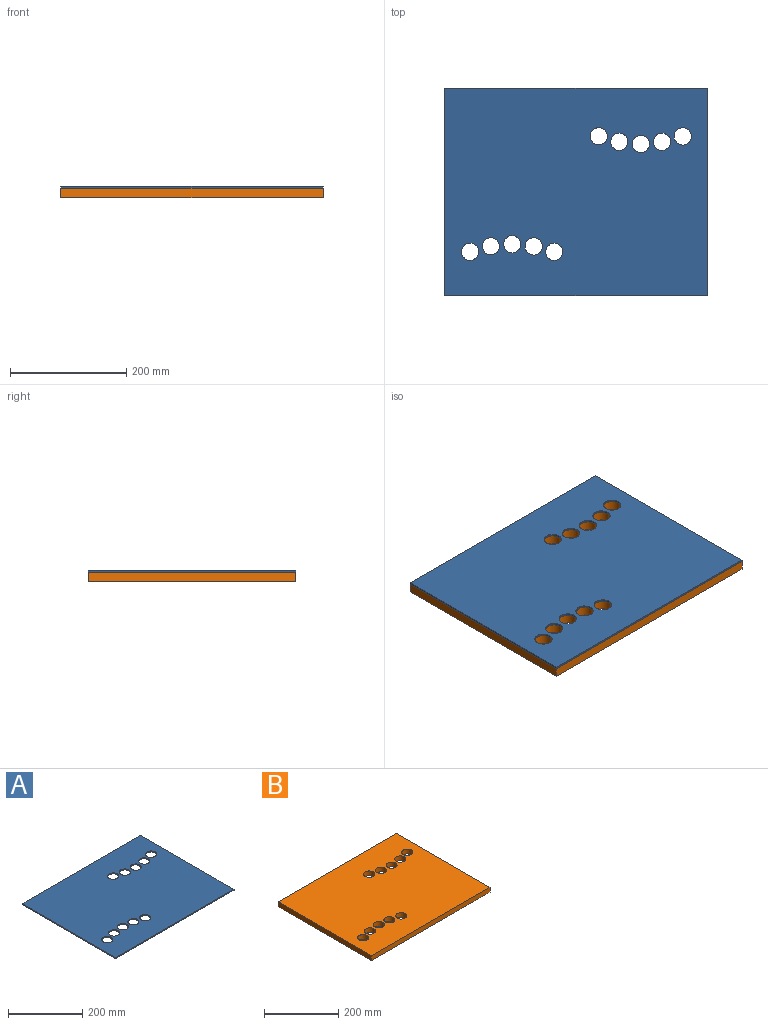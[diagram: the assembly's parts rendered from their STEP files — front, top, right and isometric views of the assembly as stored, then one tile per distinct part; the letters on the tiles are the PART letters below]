
ASSEMBLY  parts=2 mates=1
PART A: 16 faces, bbox 450.9x355.6x3.2 mm
  f0: plane 450.85x3.18mm, normal (0,1,0), area 1431.4mm2, adj f1,f8,f9,f10
  f1: plane 355.6x3.18mm, normal (-1,0,0), area 1129mm2, adj f0,f2,f9,f10
  f2: plane 450.85x3.18mm, normal (0,-1,0), area 1431.4mm2, adj f1,f8,f9,f10
  f3: cylinder r=14.87mm len=29.73mm, axis (0,0,1), area 296.6mm2, adj f9,f10
  f4: cylinder r=14.75mm len=29.5mm, axis (0,0,1), area 294.3mm2, adj f9,f10
  f5: cylinder r=14.76mm len=29.51mm, axis (0,0,1), area 294.4mm2, adj f9,f10
  f6: cylinder r=14.87mm len=29.73mm, axis (0,0,1), area 296.6mm2, adj f9,f10
  f7: cylinder r=14.8mm len=29.6mm, axis (0,0,1), area 295.3mm2, adj f9,f10
  f8: plane 355.6x3.18mm, normal (1,0,0), area 1129mm2, adj f0,f2,f9,f10
  f9: plane 450.85x355.6mm, normal (0,0,-1), area 153433.5mm2, adj f0,f1,f2,f3,f4,f5,f6,f7
  f10: plane 450.85x355.6mm, normal (0,0,1), area 153433.5mm2, adj f0,f1,f2,f3,f4,f5,f6,f7
  f11: cylinder r=14.87mm len=29.73mm, axis (0,0,1), area 296.6mm2, adj f9,f10
  f12: cylinder r=14.75mm len=29.5mm, axis (0,0,1), area 294.3mm2, adj f9,f10
  f13: cylinder r=14.76mm len=29.51mm, axis (0,0,1), area 294.4mm2, adj f9,f10
  f14: cylinder r=14.87mm len=29.73mm, axis (0,0,1), area 296.6mm2, adj f9,f10
  f15: cylinder r=14.8mm len=29.6mm, axis (0,0,1), area 295.3mm2, adj f9,f10
PART B: 16 faces, bbox 450.9x355.6x15.9 mm
  f0: plane 450.85x15.88mm, normal (0,1,0), area 7157.2mm2, adj f1,f13,f14,f15
  f1: plane 355.6x15.88mm, normal (1,0,0), area 5645.2mm2, adj f0,f2,f14,f15
  f2: plane 450.85x15.88mm, normal (0,-1,0), area 7157.2mm2, adj f1,f13,f14,f15
  f3: cylinder r=14.87mm len=29.73mm, axis (0,0,1), area 1482.8mm2, adj f14,f15
  f4: cylinder r=14.75mm len=29.5mm, axis (0,0,1), area 1471.4mm2, adj f14,f15
  f5: cylinder r=14.76mm len=29.51mm, axis (0,0,1), area 1471.8mm2, adj f14,f15
  f6: cylinder r=14.87mm len=29.73mm, axis (0,0,1), area 1482.9mm2, adj f14,f15
  f7: cylinder r=14.8mm len=29.6mm, axis (0,0,1), area 1476.3mm2, adj f14,f15
  f8: cylinder r=14.87mm len=29.73mm, axis (0,0,1), area 1482.8mm2, adj f14,f15
  f9: cylinder r=14.75mm len=29.5mm, axis (0,0,1), area 1471.4mm2, adj f14,f15
  f10: cylinder r=14.76mm len=29.51mm, axis (0,0,1), area 1471.8mm2, adj f14,f15
  f11: cylinder r=14.87mm len=29.73mm, axis (0,0,1), area 1482.9mm2, adj f14,f15
  f12: cylinder r=14.8mm len=29.6mm, axis (0,0,1), area 1476.3mm2, adj f14,f15
  f13: plane 355.6x15.88mm, normal (-1,0,0), area 5645.2mm2, adj f0,f2,f14,f15
  f14: plane 450.85x355.6mm, normal (0,0,-1), area 153433.5mm2, adj f0,f1,f2,f3,f4,f5,f6,f7
  f15: plane 450.85x355.6mm, normal (0,0,1), area 153433.5mm2, adj f0,f1,f2,f3,f4,f5,f6,f7
PLACE A t=(-88.54,-49.18,5.1)mm fixed
PLACE B t=(-88.54,-49.18,5.1)mm
MATE fastened B.f15 <-> A.f9  axis (0,0,1) through (-83.07,-45.44,1.92)mm
